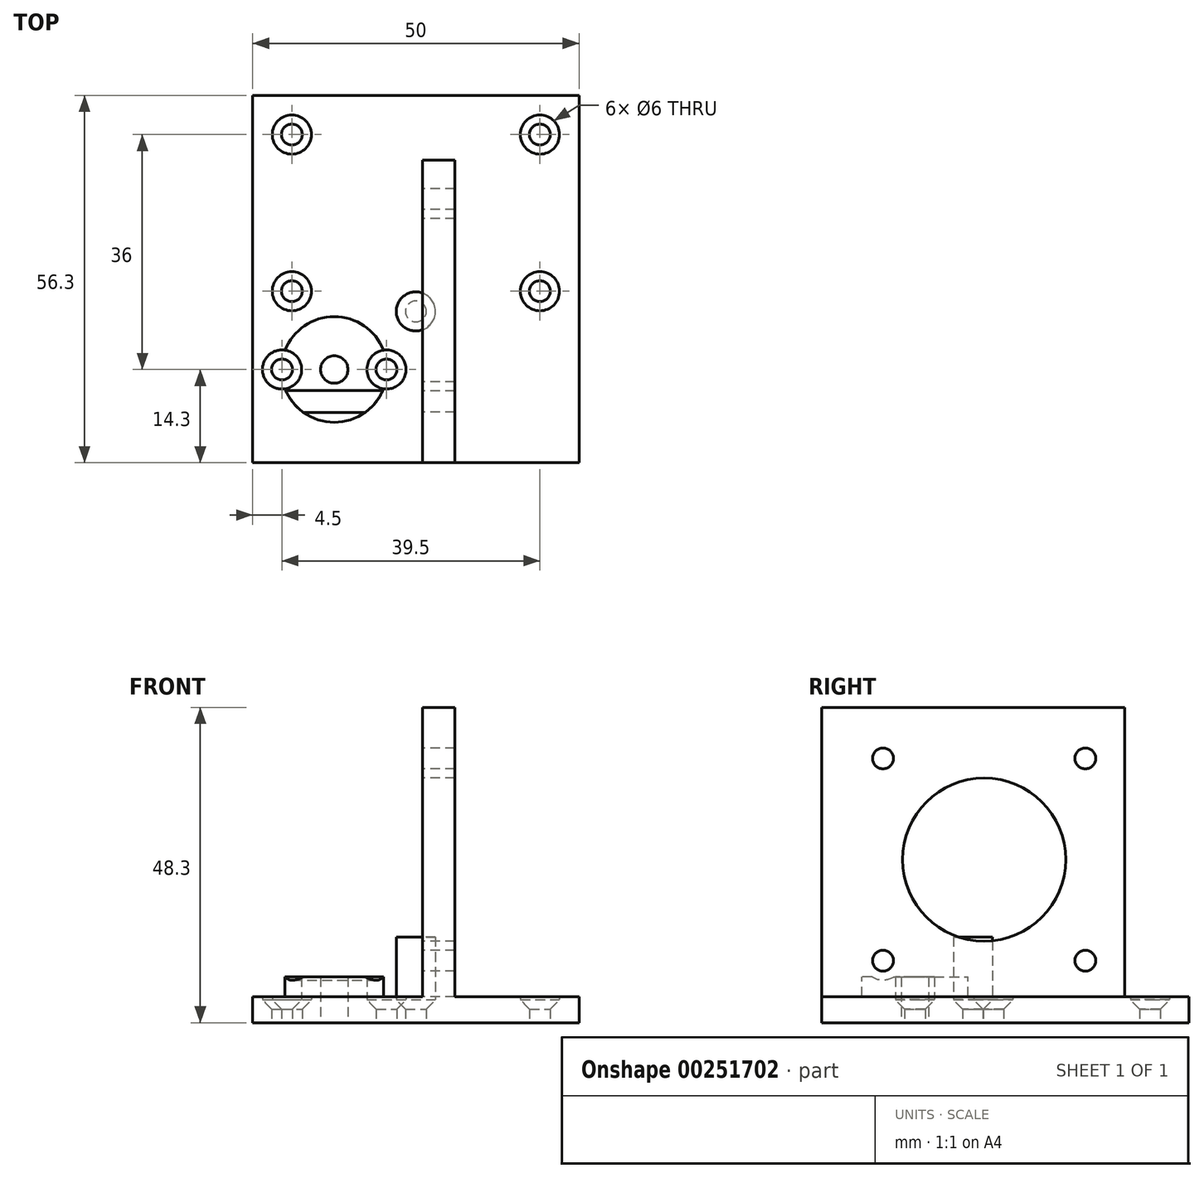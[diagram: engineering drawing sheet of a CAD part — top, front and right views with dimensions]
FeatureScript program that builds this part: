
annotation { "Feature Type Name" : "Feature", "Feature Type Description" : "" }
export const myFeature = defineFeature(function(context is Context, id is Id, definition is map)
    precondition{}
    {
        {
            var Q0;
            Q0=qCreatedBy(makeId("Top.planeOp"),FACE);
            var sketch = newSketch(context, id + "F0", { "sketchPlane" : qUnion([Q0])});
            skLineSegment(sketch, "E0.bottom", {"start": v(25, 23.2) * mm, "end": v(-25, 23.2) * mm, "construction": true});
            skLineSegment(sketch, "E0.top", {"start": v(25, -23.2) * mm, "end": v(-25, -23.2) * mm, "construction": true});
            skLineSegment(sketch, "E0.left", {"start": v(25, 23.2) * mm, "end": v(25, -23.2) * mm, "construction": true});
            skLineSegment(sketch, "E0.right", {"start": v(-25, 23.2) * mm, "end": v(-25, -23.2) * mm, "construction": true});
            skPoint(sketch, "E0.middle", {"position": v(0, 0) * mm});
            skCircle(sketch, "E1", {"center": v(-12.5, -8.9) * mm, "radius": 8 * mm, "construction": true});
            skLineSegment(sketch, "E2", {"start": v(6, 23.2) * mm, "end": v(6, -23.2) * mm, "construction": true});
            skLineSegment(sketch, "E3", {"start": v(1, 23.2) * mm, "end": v(1, -23.2) * mm, "construction": true});
            skCircle(sketch, "E4", {"center": v(-12.5, -8.9) * mm, "radius": 2 * mm, "construction": true});
            skLineSegment(sketch, "E5", {"start": v(-20.5, -8.9) * mm, "end": v(-4.5, -8.9) * mm, "construction": true});
            skCircle(sketch, "E6", {"center": v(-20.5, -8.9) * mm, "radius": 3 * mm, "construction": true});
            skCircle(sketch, "E7", {"center": v(-4.5, -8.9) * mm, "radius": 3 * mm, "construction": true});
            skLineSegment(sketch, "E8.bottom", {"start": v(-25, -2.9) * mm, "end": v(0, -2.9) * mm, "construction": true});
            skLineSegment(sketch, "E8.top", {"start": v(-25, -14.9) * mm, "end": v(0, -14.9) * mm, "construction": true});
            skLineSegment(sketch, "E8.left", {"start": v(-25, -2.9) * mm, "end": v(-25, -14.9) * mm, "construction": true});
            skLineSegment(sketch, "E8.right", {"start": v(0, -2.9) * mm, "end": v(0, -14.9) * mm, "construction": true});
            skLineSegment(sketch, "E9", {"start": v(-25, -2.9) * mm, "end": v(25, -2.9) * mm, "construction": true});
            skLineSegment(sketch, "E10", {"start": v(-25, 33.1) * mm, "end": v(25, 33.1) * mm, "construction": true});
            skLineSegment(sketch, "E11", {"start": v(-25, 33.1) * mm, "end": v(-25, 23.2) * mm, "construction": true});
            skLineSegment(sketch, "E12", {"start": v(25, 33.1) * mm, "end": v(25, 23.2) * mm, "construction": true});
            skLineSegment(sketch, "E13.bottom", {"start": v(-19, 27.1) * mm, "end": v(19, 27.1) * mm, "construction": true});
            skLineSegment(sketch, "E13.top", {"start": v(-19, 3.1) * mm, "end": v(19, 3.1) * mm, "construction": true});
            skLineSegment(sketch, "E13.left", {"start": v(-19, 27.1) * mm, "end": v(-19, 3.1) * mm, "construction": true});
            skLineSegment(sketch, "E13.right", {"start": v(19, 27.1) * mm, "end": v(19, 3.1) * mm, "construction": true});
            skLineSegment(sketch, "E14", {"start": v(19, 3.1) * mm, "end": v(19, -2.9) * mm, "construction": true});
            skLineSegment(sketch, "E15", {"start": v(19, 27.1) * mm, "end": v(19, 33.1) * mm, "construction": true});
            skCircle(sketch, "E16", {"center": v(-19, 27.1) * mm, "radius": 3 * mm, "construction": true});
            skPoint(sketch, "E17", {"position": v(-25, 0) * mm});
            skCircle(sketch, "E18", {"center": v(-19, 3.1) * mm, "radius": 3 * mm, "construction": true});
            skCircle(sketch, "E19", {"center": v(19, 27.1) * mm, "radius": 3 * mm, "construction": true});
            skCircle(sketch, "E20", {"center": v(19, 3.1) * mm, "radius": 3 * mm, "construction": true});
            skSolve(sketch);
        }
        {
            var Q0;
            Q0=qCreatedBy(makeId("Front.planeOp"),FACE);
            var sketch = newSketch(context, id + "F1", { "sketchPlane" : qUnion([Q0])});
            skLineSegment(sketch, "E21", {"start": v(0, 0) * mm, "end": v(0, 4) * mm});
            skLineSegment(sketch, "E22", {"start": v(0, 4) * mm, "end": v(0, 7) * mm});
            skLineSegment(sketch, "E23", {"start": v(0, 7) * mm, "end": v(0, 48.3) * mm});
            skSolve(sketch);
        }
        {
            var Q0;
            Q0=qCreatedBy(makeId("Top.planeOp"),FACE);
            var sketch = newSketch(context, id + "F2", { "sketchPlane" : qUnion([Q0])});
            skLineSegment(sketch, "E24.0", {"start": v(-25, 23.2) * mm, "end": v(-25, -23.2) * mm});
            skLineSegment(sketch, "E25.0", {"start": v(25, -23.2) * mm, "end": v(-25, -23.2) * mm});
            skLineSegment(sketch, "E26.0", {"start": v(25, 23.2) * mm, "end": v(25, -23.2) * mm});
            skLineSegment(sketch, "E27.0", {"start": v(-25, 33.1) * mm, "end": v(-25, 23.2) * mm});
            skLineSegment(sketch, "E28.0", {"start": v(-25, 33.1) * mm, "end": v(25, 33.1) * mm});
            skLineSegment(sketch, "E29.0", {"start": v(25, 33.1) * mm, "end": v(25, 23.2) * mm});
            skSolve(sketch);
        }
        {
            var Q0;
            Q0=makeQuery(id+"F2.imprint","IMPRINT",FACE,{"disambiguationData":[TD([[makeQuery(id+"F2.imprint","IMPRINT",EDGE,{"derivedFrom":sQuery(id+"F2.wireOp",EDGE,"E24.0")}),1.0]])]});
            var Q1;
            Q1=sQuery(id+"F1.wireOp",EDGE,"E21");
            sweep(context, id + "F3", {"profiles" : qUnion([Q0]), "path" : qUnion([Q1])});
        }
        {
            var Q0;
            Q0=qCreatedBy(makeId("Top.planeOp"),FACE);
            var sketch = newSketch(context, id + "F4", { "sketchPlane" : qUnion([Q0])});
            skLineSegment(sketch, "E30.0", {"start": v(1, 23.2) * mm, "end": v(1, -23.2) * mm});
            skLineSegment(sketch, "E31.0", {"start": v(6, 23.2) * mm, "end": v(6, -23.2) * mm});
            skLineSegment(sketch, "E32", {"start": v(1, 23.2) * mm, "end": v(6, 23.2) * mm});
            skLineSegment(sketch, "E33", {"start": v(1, -23.2) * mm, "end": v(6, -23.2) * mm});
            skSolve(sketch);
        }
        {
            var Q0;
            Q0=makeQuery(id+"F4.imprint","IMPRINT",FACE,{"disambiguationData":[TD([[makeQuery(id+"F4.imprint","IMPRINT",EDGE,{"derivedFrom":sQuery(id+"F4.wireOp",EDGE,"E30.0")}),1.0]])]});
            var Q1;
            Q1=sQuery(id+"F1.wireOp",EDGE,"E21");
            var Q2;
            Q2=sQuery(id+"F1.wireOp",EDGE,"E22");
            var Q3;
            Q3=sQuery(id+"F1.wireOp",EDGE,"E23");
            sweep(context, id + "F5", {"operationType" : NewBodyOperationType.ADD, "profiles" : qUnion([Q0]), "path" : qUnion([Q1, Q2, Q3])});
        }
        {
            var Q0;
            Q0=qCreatedBy(makeId("Top.planeOp"),FACE);
            var sketch = newSketch(context, id + "F6", { "sketchPlane" : qUnion([Q0])});
            skCircle(sketch, "E34.0", {"center": v(-12.5, -8.9) * mm, "radius": 8 * mm, "construction": true});
            skCircle(sketch, "E35.0", {"center": v(-12.5, -8.9) * mm, "radius": 8.1 * mm});
            skSolve(sketch);
        }
        {
            var Q0;
            Q0=makeQuery(id+"F6.imprint","IMPRINT",FACE,{"disambiguationData":[TD([[makeQuery(id+"F6.imprint","IMPRINT",EDGE,{"derivedFrom":sQuery(id+"F6.wireOp",EDGE,"E35.0")}),1.0]])]});
            var Q1;
            Q1=sQuery(id+"F1.wireOp",EDGE,"E21");
            var Q2;
            Q2=sQuery(id+"F1.wireOp",EDGE,"E22");
            sweep(context, id + "F7", {"operationType" : NewBodyOperationType.ADD, "profiles" : qUnion([Q0]), "path" : qUnion([Q1, Q2])});
        }
        {
            var Q0;
            Q0=makeQuery(id+"F5.opSweep","SWEPT_FACE",FACE,{"disambiguationData":[OSD([sQuery(id+"F1.wireOp",EDGE,"E21"),sQuery(id+"F4.wireOp",EDGE,"E30.0")])]});
            var sketch = newSketch(context, id + "F8", { "sketchPlane" : qUnion([Q0])});
            skLineSegment(sketch, "E36.0.0", {"start": v(-23.2, 48.3) * mm, "end": v(-23.2, 4) * mm, "construction": true});
            skLineSegment(sketch, "E36.0.1", {"start": v(-23.2, 4) * mm, "end": v(23.2, 4) * mm, "construction": true});
            skLineSegment(sketch, "E36.0.2", {"start": v(23.2, 4) * mm, "end": v(23.2, 48.3) * mm, "construction": true});
            skLineSegment(sketch, "E36.0.3", {"start": v(23.2, 48.3) * mm, "end": v(-23.2, 48.3) * mm, "construction": true});
            skLineSegment(sketch, "E37.0", {"start": v(6.9, 0) * mm, "end": v(10.9, 0) * mm, "construction": true});
            skLineSegment(sketch, "E38.bottom", {"start": v(13.8, 40.5) * mm, "end": v(-17.2, 40.5) * mm, "construction": true});
            skLineSegment(sketch, "E38.top", {"start": v(13.8, 9.5) * mm, "end": v(-17.2, 9.5) * mm, "construction": true});
            skLineSegment(sketch, "E38.left", {"start": v(13.8, 40.5) * mm, "end": v(13.8, 9.5) * mm, "construction": true});
            skLineSegment(sketch, "E38.right", {"start": v(-17.2, 40.5) * mm, "end": v(-17.2, 9.5) * mm, "construction": true});
            skPoint(sketch, "E38.middle", {"position": v(-1.7, 25) * mm});
            skPoint(sketch, "E39", {"position": v(8.9, 0) * mm});
            skCircle(sketch, "E40", {"center": v(-1.7, 25) * mm, "radius": 12.5 * mm});
            skCircle(sketch, "E41", {"center": v(-17.2, 40.5) * mm, "radius": 1.6 * mm});
            skCircle(sketch, "E42", {"center": v(13.8, 40.5) * mm, "radius": 1.6 * mm});
            skCircle(sketch, "E43", {"center": v(13.8, 9.5) * mm, "radius": 1.6 * mm});
            skCircle(sketch, "E44", {"center": v(-17.2, 9.5) * mm, "radius": 1.6 * mm});
            skSolve(sketch);
        }
        {
            var Q0;
            Q0 = qSketchRegion(id + "F8", true);
            var Q1;
            Q1=makeQuery(id+"F5.opSweep","SWEPT_FACE",FACE,{"disambiguationData":[OSD([sQuery(id+"F1.wireOp",EDGE,"E21"),sQuery(id+"F4.wireOp",EDGE,"E31.0")])]});
            extrude(context, id + "F9", {"entities" : qUnion([Q0]), "operationType" : NewBodyOperationType.REMOVE, "endBound" : BoundingType.UP_TO_SURFACE, "oppositeDirection" : true, "endBoundEntityFace" : qUnion([Q1]), "depth" : 25 * mm});
        }
        {
            var Q0;
            Q0=qCreatedBy(makeId("Top.planeOp"),FACE);
            var sketch = newSketch(context, id + "F10", { "sketchPlane" : qUnion([Q0])});
            skCircle(sketch, "E45.0", {"center": v(-12.5, -8.9) * mm, "radius": 2 * mm, "construction": true});
            skCircle(sketch, "E46.0", {"center": v(-12.5, -8.9) * mm, "radius": 2.1 * mm});
            skSolve(sketch);
        }
        {
            var Q0;
            Q0 = qSketchRegion(id + "F10", true);
            var Q1;
            Q1=makeQuery(id+"F7.opSweep","CAP_FACE",FACE,{"disambiguationData":[OSD([sQuery(id+"F1.wireOp",VERTEX,"E22.end"),sQuery(id+"F6.wireOp",EDGE,"E35.0")])],"isStart":false});
            extrude(context, id + "F11", {"entities" : qUnion([Q0]), "operationType" : NewBodyOperationType.REMOVE, "endBound" : BoundingType.UP_TO_SURFACE, "endBoundEntityFace" : qUnion([Q1]), "depth" : 25 * mm});
        }
        {
            var Q0;
            Q0=makeQuery(id+"F5.opSweep","SWEPT_FACE",FACE,{"disambiguationData":[OSD([sQuery(id+"F1.wireOp",EDGE,"E21"),sQuery(id+"F4.wireOp",EDGE,"E30.0")])]});
            var sketch = newSketch(context, id + "F12", { "sketchPlane" : qUnion([Q0])});
            skCircle(sketch, "E47.0", {"center": v(13.8, 9.5) * mm, "radius": 1.6 * mm, "construction": true});
            skCircle(sketch, "E48", {"center": v(13.8, 9.5) * mm, "radius": 3 * mm});
            skSolve(sketch);
        }
        {
            var Q0;
            Q0 = qSketchRegion(id + "F12", true);
            var Q1;
            Q1=makeQuery(id+"F3.opSweep","SWEPT_FACE",FACE,{"disambiguationData":[OSD([sQuery(id+"F1.wireOp",EDGE,"E21"),sQuery(id+"F2.wireOp",EDGE,"E24.0"),sQuery(id+"F2.wireOp",EDGE,"E27.0")])]});
            extrude(context, id + "F13", {"entities" : qUnion([Q0]), "operationType" : NewBodyOperationType.REMOVE, "endBound" : BoundingType.UP_TO_SURFACE, "endBoundEntityFace" : qUnion([Q1]), "depth" : 25 * mm});
        }
        {
            var Q0;
            Q0=qCreatedBy(makeId("Right.planeOp"),FACE);
            var sketch = newSketch(context, id + "F14", { "sketchPlane" : qUnion([Q0])});
            skLineSegment(sketch, "E49.0", {"start": v(0, 0) * mm, "end": v(0, 4) * mm});
            skLineSegment(sketch, "E50", {"start": v(-3, 4) * mm, "end": v(-3, 3.5) * mm});
            skLineSegment(sketch, "E51", {"start": v(-3, 3.5) * mm, "end": v(-1.6, 2.1) * mm});
            skLineSegment(sketch, "E52", {"start": v(-1.6, 2.1) * mm, "end": v(-1.6, 0) * mm});
            skLineSegment(sketch, "E53", {"start": v(-1.6, 0) * mm, "end": v(0, 0) * mm});
            skLineSegment(sketch, "E54", {"start": v(-3, 4) * mm, "end": v(-3, 13.13) * mm});
            skLineSegment(sketch, "E55", {"start": v(-3, 13.13) * mm, "end": v(0, 13.13) * mm});
            skLineSegment(sketch, "E56", {"start": v(0, 13.13) * mm, "end": v(0, 4) * mm});
            skSolve(sketch);
        }
        {
            var Q0;
            Q0=makeQuery(id+"F14.imprint","IMPRINT",FACE,{"disambiguationData":[TD([[makeQuery(id+"F14.imprint","IMPRINT",EDGE,{"derivedFrom":sQuery(id+"F14.wireOp",EDGE,"E49.0")}),1.0]])]});
            var Q1;
            Q1=sQuery(id+"F14.wireOp",EDGE,"E49.0");
            revolve(context, id + "F15", {"entities" : qUnion([Q0]), "axis" : qUnion([Q1]), "revolveType" : RevolveType.FULL});
        }
        {
            var Q0;
            Q0=makeQuery(id+"F15.opRevolve","SWEPT_BODY",BODY,{"disambiguationData":[OSD([sQuery(id+"F14.wireOp",EDGE,"E49.0"),sQuery(id+"F14.wireOp",EDGE,"E50"),sQuery(id+"F14.wireOp",EDGE,"E51"),sQuery(id+"F14.wireOp",EDGE,"E52"),sQuery(id+"F14.wireOp",EDGE,"E53"),sQuery(id+"F14.wireOp",EDGE,"E54"),sQuery(id+"F14.wireOp",EDGE,"E55"),sQuery(id+"F14.wireOp",EDGE,"E56")])]});
            var Q1;
            Q1=sQuery(id+"F0.wireOp",VERTEX,"E0.middle");
            var Q2;
            Q2=sQuery(id+"F0.wireOp",VERTEX,"E5.start");
            transform(context, id + "F16", {"entities" : qUnion([Q0]), "transformType" : TransformType.TRANSLATION_ENTITY, "oppositeDirectionEntity" : false, "transformLine" : qUnion([Q1, Q2]), "makeCopy" : true});
        }
        {
            var Q0;
            Q0=makeQuery(id+"F15.opRevolve","SWEPT_BODY",BODY,{"disambiguationData":[OSD([sQuery(id+"F14.wireOp",EDGE,"E49.0"),sQuery(id+"F14.wireOp",EDGE,"E50"),sQuery(id+"F14.wireOp",EDGE,"E51"),sQuery(id+"F14.wireOp",EDGE,"E52"),sQuery(id+"F14.wireOp",EDGE,"E53"),sQuery(id+"F14.wireOp",EDGE,"E54"),sQuery(id+"F14.wireOp",EDGE,"E55"),sQuery(id+"F14.wireOp",EDGE,"E56")])]});
            var Q1;
            Q1=sQuery(id+"F0.wireOp",VERTEX,"E0.middle");
            var Q2;
            Q2=sQuery(id+"F0.wireOp",VERTEX,"E7.center");
            transform(context, id + "F17", {"entities" : qUnion([Q0]), "transformType" : TransformType.TRANSLATION_ENTITY, "oppositeDirectionEntity" : false, "transformLine" : qUnion([Q1, Q2]), "makeCopy" : true});
        }
        {
            var Q0;
            Q0=makeQuery(id+"F15.opRevolve","SWEPT_BODY",BODY,{"disambiguationData":[OSD([sQuery(id+"F14.wireOp",EDGE,"E49.0"),sQuery(id+"F14.wireOp",EDGE,"E50"),sQuery(id+"F14.wireOp",EDGE,"E51"),sQuery(id+"F14.wireOp",EDGE,"E52"),sQuery(id+"F14.wireOp",EDGE,"E53"),sQuery(id+"F14.wireOp",EDGE,"E54"),sQuery(id+"F14.wireOp",EDGE,"E55"),sQuery(id+"F14.wireOp",EDGE,"E56")])]});
            var Q1;
            Q1=sQuery(id+"F0.wireOp",VERTEX,"E0.middle");
            var Q2;
            Q2=sQuery(id+"F0.wireOp",VERTEX,"E18.center");
            transform(context, id + "F18", {"entities" : qUnion([Q0]), "transformType" : TransformType.TRANSLATION_ENTITY, "oppositeDirectionEntity" : false, "transformLine" : qUnion([Q1, Q2]), "makeCopy" : true});
        }
        {
            var Q0;
            Q0=makeQuery(id+"F15.opRevolve","SWEPT_BODY",BODY,{"disambiguationData":[OSD([sQuery(id+"F14.wireOp",EDGE,"E49.0"),sQuery(id+"F14.wireOp",EDGE,"E50"),sQuery(id+"F14.wireOp",EDGE,"E51"),sQuery(id+"F14.wireOp",EDGE,"E52"),sQuery(id+"F14.wireOp",EDGE,"E53"),sQuery(id+"F14.wireOp",EDGE,"E54"),sQuery(id+"F14.wireOp",EDGE,"E55"),sQuery(id+"F14.wireOp",EDGE,"E56")])]});
            var Q1;
            Q1=sQuery(id+"F0.wireOp",VERTEX,"E0.middle");
            var Q2;
            Q2=sQuery(id+"F0.wireOp",VERTEX,"E13.left.start");
            transform(context, id + "F19", {"entities" : qUnion([Q0]), "transformType" : TransformType.TRANSLATION_ENTITY, "oppositeDirectionEntity" : false, "transformLine" : qUnion([Q1, Q2]), "makeCopy" : true});
        }
        {
            var Q0;
            Q0=makeQuery(id+"F15.opRevolve","SWEPT_BODY",BODY,{"disambiguationData":[OSD([sQuery(id+"F14.wireOp",EDGE,"E49.0"),sQuery(id+"F14.wireOp",EDGE,"E50"),sQuery(id+"F14.wireOp",EDGE,"E51"),sQuery(id+"F14.wireOp",EDGE,"E52"),sQuery(id+"F14.wireOp",EDGE,"E53"),sQuery(id+"F14.wireOp",EDGE,"E54"),sQuery(id+"F14.wireOp",EDGE,"E55"),sQuery(id+"F14.wireOp",EDGE,"E56")])]});
            var Q1;
            Q1=sQuery(id+"F0.wireOp",VERTEX,"E0.middle");
            var Q2;
            Q2=sQuery(id+"F0.wireOp",VERTEX,"E13.bottom.end");
            transform(context, id + "F20", {"entities" : qUnion([Q0]), "transformType" : TransformType.TRANSLATION_ENTITY, "oppositeDirectionEntity" : false, "transformLine" : qUnion([Q1, Q2]), "makeCopy" : true});
        }
        {
            var Q0;
            Q0=makeQuery(id+"F15.opRevolve","SWEPT_BODY",BODY,{"disambiguationData":[OSD([sQuery(id+"F14.wireOp",EDGE,"E49.0"),sQuery(id+"F14.wireOp",EDGE,"E50"),sQuery(id+"F14.wireOp",EDGE,"E51"),sQuery(id+"F14.wireOp",EDGE,"E52"),sQuery(id+"F14.wireOp",EDGE,"E53"),sQuery(id+"F14.wireOp",EDGE,"E54"),sQuery(id+"F14.wireOp",EDGE,"E55"),sQuery(id+"F14.wireOp",EDGE,"E56")])]});
            var Q1;
            Q1=sQuery(id+"F0.wireOp",VERTEX,"E0.middle");
            var Q2;
            Q2=sQuery(id+"F0.wireOp",VERTEX,"E13.top.end");
            transform(context, id + "F21", {"entities" : qUnion([Q0]), "transformType" : TransformType.TRANSLATION_ENTITY, "oppositeDirectionEntity" : false, "transformLine" : qUnion([Q1, Q2]), "makeCopy" : true});
        }
        {
            var Q0;
            Q0=makeQuery(id+"F16.opPattern","COPY",BODY,{"derivedFrom":makeQuery(id+"F15.opRevolve","SWEPT_BODY",BODY,{"disambiguationData":[OSD([sQuery(id+"F14.wireOp",EDGE,"E49.0"),sQuery(id+"F14.wireOp",EDGE,"E50"),sQuery(id+"F14.wireOp",EDGE,"E51"),sQuery(id+"F14.wireOp",EDGE,"E52"),sQuery(id+"F14.wireOp",EDGE,"E53"),sQuery(id+"F14.wireOp",EDGE,"E54"),sQuery(id+"F14.wireOp",EDGE,"E55"),sQuery(id+"F14.wireOp",EDGE,"E56")])]}),"instanceName":"1"});
            var Q1;
            Q1=makeQuery(id+"F17.opPattern","COPY",BODY,{"derivedFrom":makeQuery(id+"F15.opRevolve","SWEPT_BODY",BODY,{"disambiguationData":[OSD([sQuery(id+"F14.wireOp",EDGE,"E49.0"),sQuery(id+"F14.wireOp",EDGE,"E50"),sQuery(id+"F14.wireOp",EDGE,"E51"),sQuery(id+"F14.wireOp",EDGE,"E52"),sQuery(id+"F14.wireOp",EDGE,"E53"),sQuery(id+"F14.wireOp",EDGE,"E54"),sQuery(id+"F14.wireOp",EDGE,"E55"),sQuery(id+"F14.wireOp",EDGE,"E56")])]}),"instanceName":"1"});
            var Q2;
            Q2=makeQuery(id+"F19.opPattern","COPY",BODY,{"derivedFrom":makeQuery(id+"F15.opRevolve","SWEPT_BODY",BODY,{"disambiguationData":[OSD([sQuery(id+"F14.wireOp",EDGE,"E49.0"),sQuery(id+"F14.wireOp",EDGE,"E50"),sQuery(id+"F14.wireOp",EDGE,"E51"),sQuery(id+"F14.wireOp",EDGE,"E52"),sQuery(id+"F14.wireOp",EDGE,"E53"),sQuery(id+"F14.wireOp",EDGE,"E54"),sQuery(id+"F14.wireOp",EDGE,"E55"),sQuery(id+"F14.wireOp",EDGE,"E56")])]}),"instanceName":"1"});
            var Q3;
            Q3=makeQuery(id+"F18.opPattern","COPY",BODY,{"derivedFrom":makeQuery(id+"F15.opRevolve","SWEPT_BODY",BODY,{"disambiguationData":[OSD([sQuery(id+"F14.wireOp",EDGE,"E49.0"),sQuery(id+"F14.wireOp",EDGE,"E50"),sQuery(id+"F14.wireOp",EDGE,"E51"),sQuery(id+"F14.wireOp",EDGE,"E52"),sQuery(id+"F14.wireOp",EDGE,"E53"),sQuery(id+"F14.wireOp",EDGE,"E54"),sQuery(id+"F14.wireOp",EDGE,"E55"),sQuery(id+"F14.wireOp",EDGE,"E56")])]}),"instanceName":"1"});
            var Q4;
            Q4=makeQuery(id+"F21.opPattern","COPY",BODY,{"derivedFrom":makeQuery(id+"F15.opRevolve","SWEPT_BODY",BODY,{"disambiguationData":[OSD([sQuery(id+"F14.wireOp",EDGE,"E49.0"),sQuery(id+"F14.wireOp",EDGE,"E50"),sQuery(id+"F14.wireOp",EDGE,"E51"),sQuery(id+"F14.wireOp",EDGE,"E52"),sQuery(id+"F14.wireOp",EDGE,"E53"),sQuery(id+"F14.wireOp",EDGE,"E54"),sQuery(id+"F14.wireOp",EDGE,"E55"),sQuery(id+"F14.wireOp",EDGE,"E56")])]}),"instanceName":"1"});
            var Q5;
            Q5=makeQuery(id+"F20.opPattern","COPY",BODY,{"derivedFrom":makeQuery(id+"F15.opRevolve","SWEPT_BODY",BODY,{"disambiguationData":[OSD([sQuery(id+"F14.wireOp",EDGE,"E49.0"),sQuery(id+"F14.wireOp",EDGE,"E50"),sQuery(id+"F14.wireOp",EDGE,"E51"),sQuery(id+"F14.wireOp",EDGE,"E52"),sQuery(id+"F14.wireOp",EDGE,"E53"),sQuery(id+"F14.wireOp",EDGE,"E54"),sQuery(id+"F14.wireOp",EDGE,"E55"),sQuery(id+"F14.wireOp",EDGE,"E56")])]}),"instanceName":"1"});
            var Q6;
            Q6=makeQuery(id+"F3.opSweep","SWEPT_BODY",BODY,{"disambiguationData":[OSD([sQuery(id+"F1.wireOp",EDGE,"E21"),sQuery(id+"F2.wireOp",EDGE,"E24.0"),sQuery(id+"F2.wireOp",EDGE,"E25.0"),sQuery(id+"F2.wireOp",EDGE,"E26.0"),sQuery(id+"F2.wireOp",EDGE,"E27.0"),sQuery(id+"F2.wireOp",EDGE,"E28.0"),sQuery(id+"F2.wireOp",EDGE,"E29.0")])]});
            booleanBodies(context, id + "F22", {"operationType" : BooleanOperationType.SUBTRACTION, "tools" : qUnion([Q0, Q1, Q2, Q3, Q4, Q5]), "targets" : qUnion([Q6])});
        }
    });
